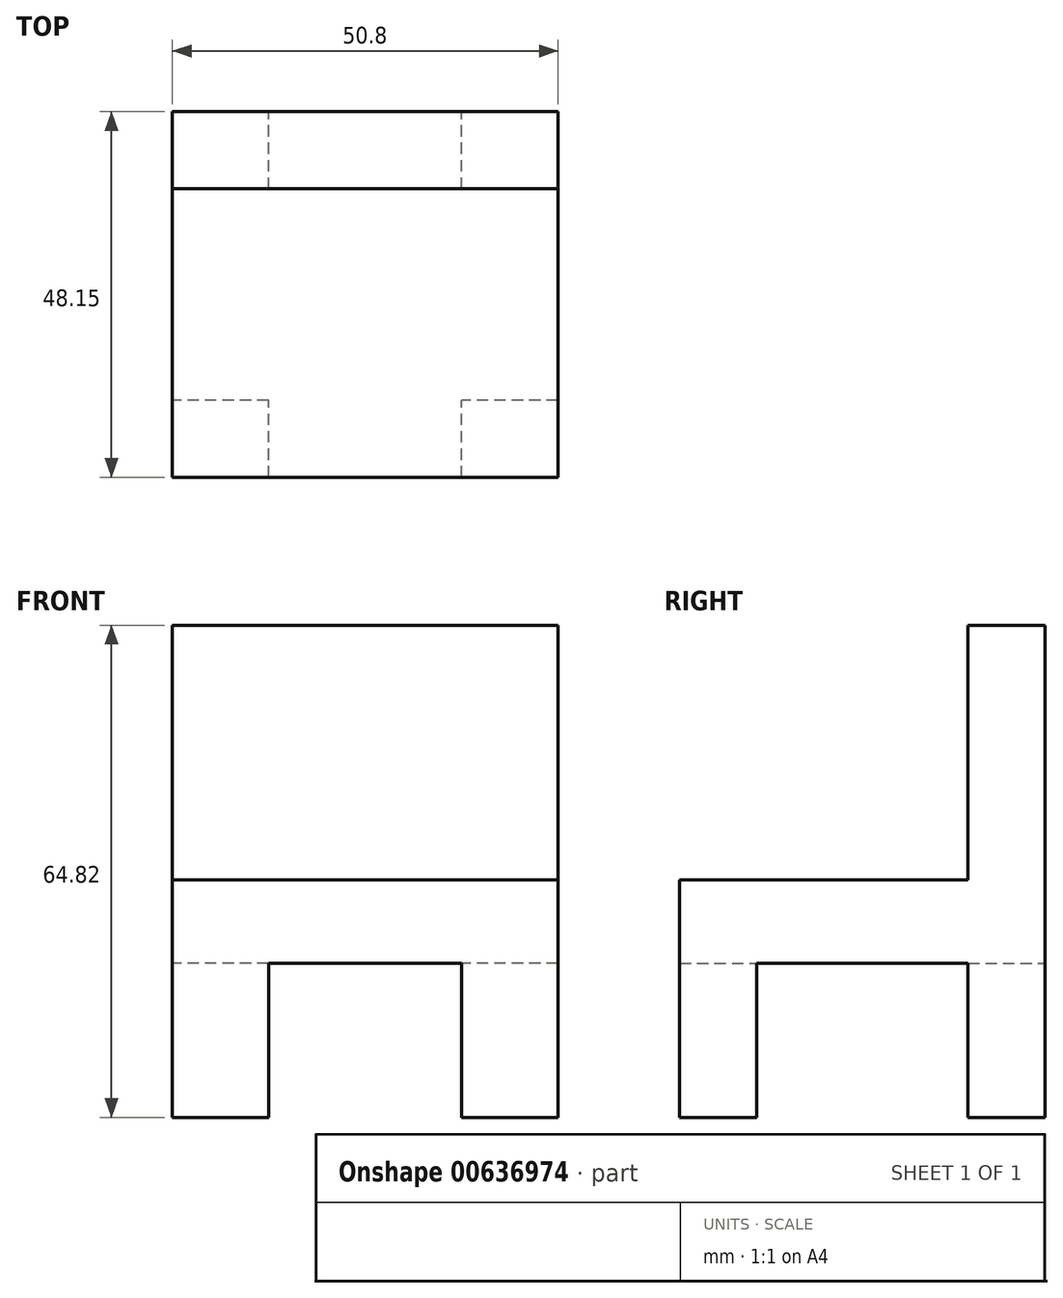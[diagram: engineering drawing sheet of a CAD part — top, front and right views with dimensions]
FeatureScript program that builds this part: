
annotation { "Feature Type Name" : "Feature", "Feature Type Description" : "" }
export const myFeature = defineFeature(function(context is Context, id is Id, definition is map)
    precondition{}
    {
        {
            var Q0;
            Q0=qCreatedBy(makeId("Right.planeOp"),FACE);
            var sketch = newSketch(context, id + "F0", { "sketchPlane" : qUnion([Q0])});
            skLineSegment(sketch, "E0.bottom", {"start": v(48.28, 51.96) * mm, "end": v(38.12, 51.96) * mm});
            skLineSegment(sketch, "E0.top", {"start": v(48.28, 18.43) * mm, "end": v(38.12, 18.43) * mm});
            skLineSegment(sketch, "E0.left", {"start": v(48.28, 51.96) * mm, "end": v(48.28, 18.43) * mm});
            skLineSegment(sketch, "E0.right", {"start": v(38.12, 51.96) * mm, "end": v(38.12, 18.43) * mm});
            skLineSegment(sketch, "E1.bottom", {"start": v(48.28, 18.43) * mm, "end": v(0.13, 18.43) * mm});
            skLineSegment(sketch, "E1.top", {"start": v(48.28, 7.46) * mm, "end": v(0.13, 7.46) * mm});
            skLineSegment(sketch, "E1.left", {"start": v(48.28, 18.43) * mm, "end": v(48.28, 7.46) * mm});
            skLineSegment(sketch, "E1.right", {"start": v(0.13, 18.43) * mm, "end": v(0.13, 7.46) * mm});
            skLineSegment(sketch, "E2.bottom", {"start": v(48.28, 7.46) * mm, "end": v(38.12, 7.46) * mm});
            skLineSegment(sketch, "E2.top", {"start": v(48.28, -12.86) * mm, "end": v(38.12, -12.86) * mm});
            skLineSegment(sketch, "E2.left", {"start": v(48.28, 7.46) * mm, "end": v(48.28, -12.86) * mm});
            skLineSegment(sketch, "E2.right", {"start": v(38.12, 7.46) * mm, "end": v(38.12, -12.86) * mm});
            skLineSegment(sketch, "E3.bottom", {"start": v(0.13, 7.46) * mm, "end": v(10.29, 7.46) * mm});
            skLineSegment(sketch, "E3.top", {"start": v(0.13, -12.86) * mm, "end": v(10.29, -12.86) * mm});
            skLineSegment(sketch, "E3.left", {"start": v(0.13, 7.46) * mm, "end": v(0.13, -12.86) * mm});
            skLineSegment(sketch, "E3.right", {"start": v(10.29, 7.46) * mm, "end": v(10.29, -12.86) * mm});
            skSolve(sketch);
        }
        {
            var Q0;
            Q0 = qSketchRegion(id + "F0", true);
            extrude(context, id + "F1", {"entities" : qUnion([Q0]), "depth" : 50.8 * mm, "offsetDistance" : 25.4 * mm});
        }
        {
            var Q0;
            Q0=makeQuery(id+"F1.opExtrude","SWEPT_FACE",FACE,{"disambiguationData":[OSD([sQuery(id+"F0.wireOp",EDGE,"E0.left"),sQuery(id+"F0.wireOp",EDGE,"E1.left"),sQuery(id+"F0.wireOp",EDGE,"E2.left")])]});
            var sketch = newSketch(context, id + "F2", { "sketchPlane" : qUnion([Q0])});
            skLineSegment(sketch, "E4", {"start": v(-50.8, -12.86) * mm, "end": v(-38.1, -12.86) * mm});
            skLineSegment(sketch, "E5", {"start": v(-38.1, -12.86) * mm, "end": v(-12.7, -12.86) * mm});
            skLineSegment(sketch, "E6.left", {"start": v(-38.1, -12.86) * mm, "end": v(-38.1, -12.86) * mm});
            skLineSegment(sketch, "E6.right", {"start": v(-12.7, -12.86) * mm, "end": v(-12.7, -12.86) * mm});
            skLineSegment(sketch, "E7.top", {"start": v(-38.1, 7.46) * mm, "end": v(-12.7, 7.46) * mm});
            skLineSegment(sketch, "E7.left", {"start": v(-38.1, -12.86) * mm, "end": v(-38.1, 7.46) * mm});
            skLineSegment(sketch, "E7.right", {"start": v(-12.7, -12.86) * mm, "end": v(-12.7, 7.46) * mm});
            skSolve(sketch);
        }
        {
            var Q0;
            Q0 = qSketchRegion(id + "F2", true);
            extrude(context, id + "F3", {"entities" : qUnion([Q0]), "operationType" : NewBodyOperationType.REMOVE, "oppositeDirection" : true, "depth" : 73.9 * mm, "offsetDistance" : 25.4 * mm});
        }
    });
